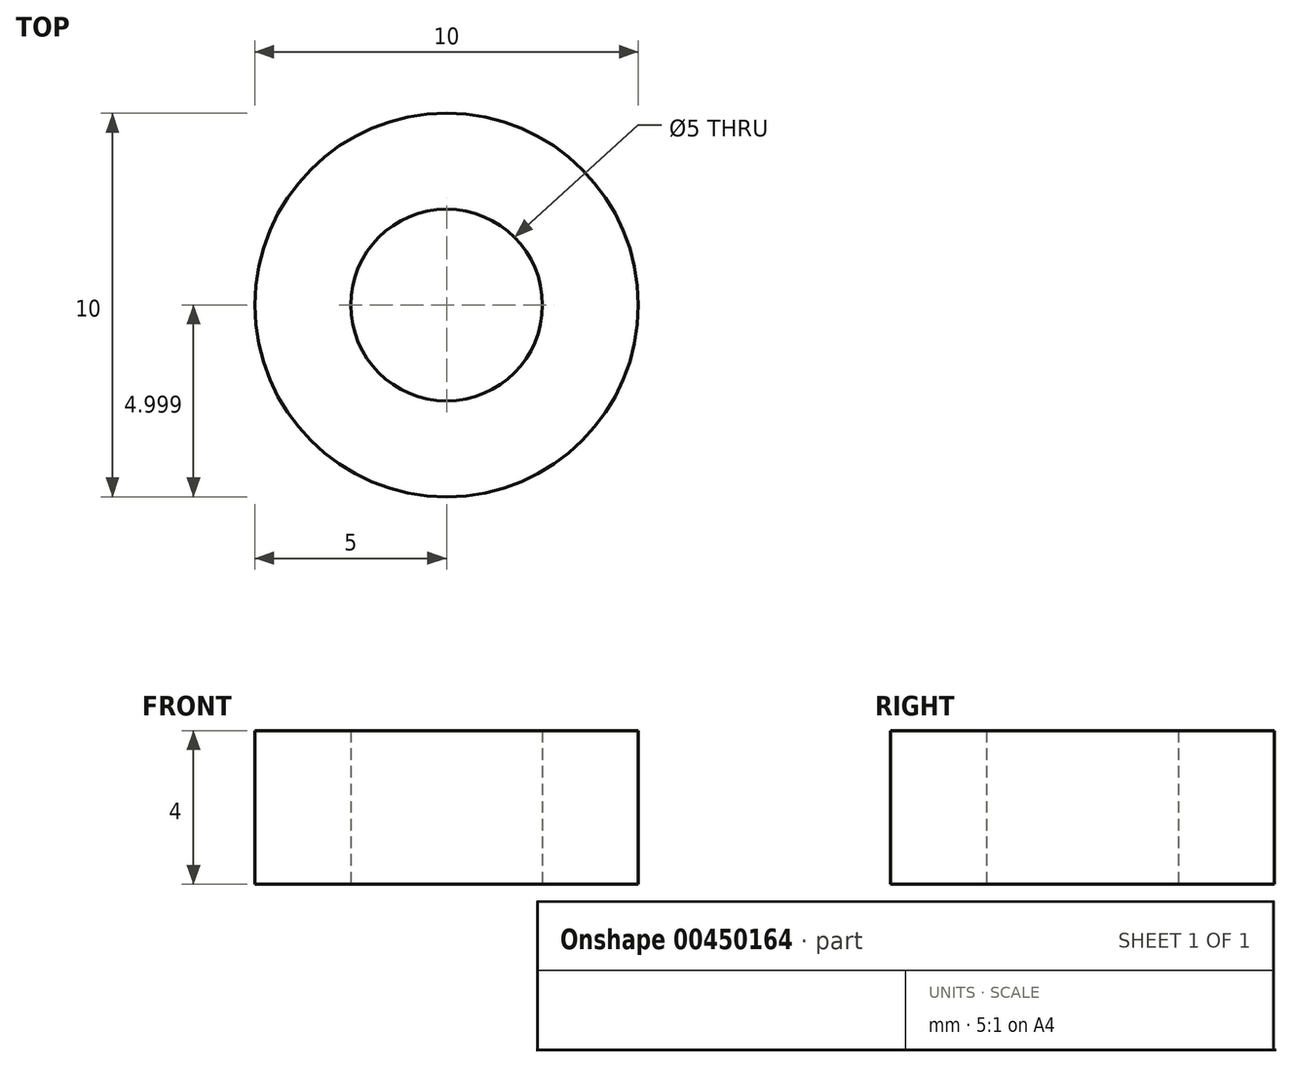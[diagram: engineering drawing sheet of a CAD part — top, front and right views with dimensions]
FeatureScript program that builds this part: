
annotation { "Feature Type Name" : "Feature", "Feature Type Description" : "" }
export const myFeature = defineFeature(function(context is Context, id is Id, definition is map)
    precondition{}
    {
        {
            var Q0;
            Q0=qCreatedBy(makeId("Top.planeOp"),FACE);
            var sketch = newSketch(context, id + "F0", { "sketchPlane" : qUnion([Q0])});
            skCircle(sketch, "E0", {"center": v(0, 0.17) * mm, "radius": 2.5 * mm});
            skCircle(sketch, "E1", {"center": v(0, 0.17) * mm, "radius": 5 * mm});
            skSolve(sketch);
        }
        {
            var Q0;
            Q0 = qSketchRegion(id + "F0", true);
            extrude(context, id + "F1", {"entities" : qUnion([Q0]), "depth" : 4 * mm});
        }
    });
